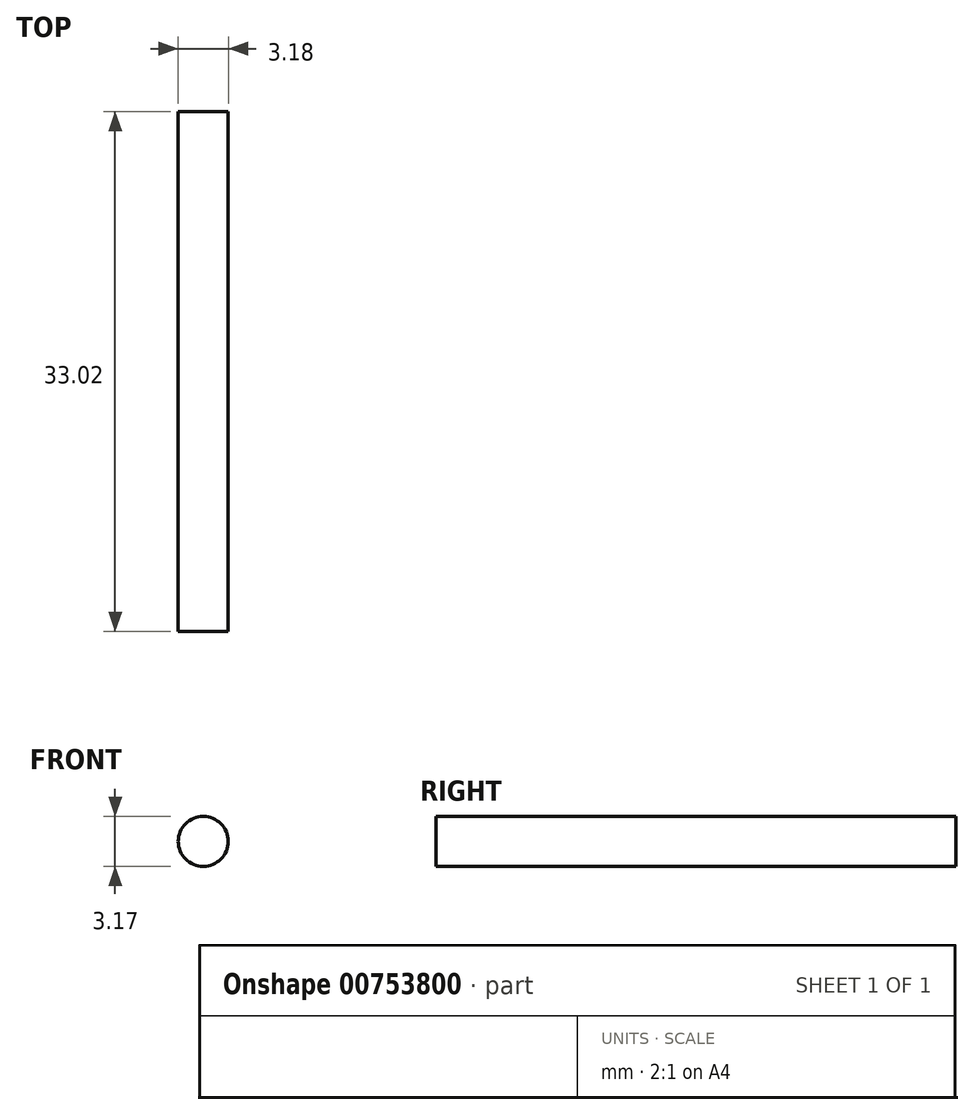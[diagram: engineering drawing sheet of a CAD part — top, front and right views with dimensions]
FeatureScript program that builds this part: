
annotation { "Feature Type Name" : "Feature", "Feature Type Description" : "" }
export const myFeature = defineFeature(function(context is Context, id is Id, definition is map)
    precondition{}
    {
        {
            var Q0;
            Q0=qCreatedBy(makeId("Front.planeOp"),FACE);
            var sketch = newSketch(context, id + "F0", { "sketchPlane" : qUnion([Q0])});
            skCircle(sketch, "E0", {"center": v(-59.7, 53.67) * mm, "radius": 1.59 * mm});
            skSolve(sketch);
        }
        {
            var Q0;
            Q0=makeQuery(id+"F0.imprint","IMPRINT",FACE,{"disambiguationData":[TD([[makeQuery(id+"F0.imprint","IMPRINT",EDGE,{"derivedFrom":sQuery(id+"F0.wireOp",EDGE,"E0")}),1.0]])]});
            extrude(context, id + "F1", {"entities" : qUnion([Q0]), "depth" : 33.02 * mm, "offsetDistance" : 25.4 * mm});
        }
    });
